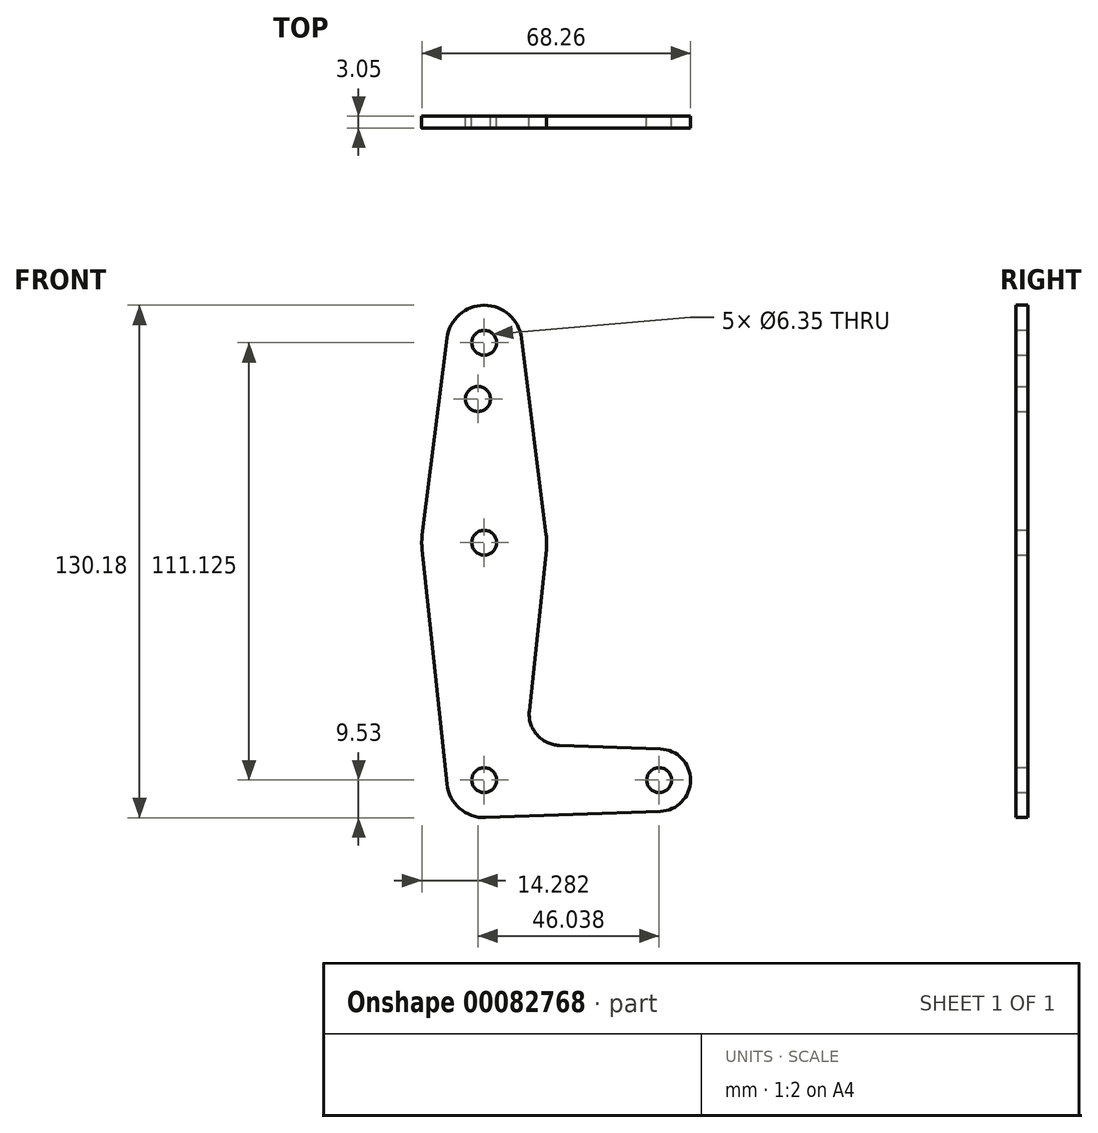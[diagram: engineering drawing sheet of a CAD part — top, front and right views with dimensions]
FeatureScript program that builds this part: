
annotation { "Feature Type Name" : "Feature", "Feature Type Description" : "" }
export const myFeature = defineFeature(function(context is Context, id is Id, definition is map)
    precondition{}
    {
        {
            var Q0;
            Q0=qCreatedBy(makeId("Front.planeOp"),FACE);
            var sketch = newSketch(context, id + "F0", { "sketchPlane" : qUnion([Q0])});
            skCircle(sketch, "E0", {"center": v(0, 111.13) * mm, "radius": 9.52 * mm});
            skCircle(sketch, "E1", {"center": v(0, 60.33) * mm, "radius": 15.88 * mm});
            skCircle(sketch, "E2", {"center": v(0, 0) * mm, "radius": 9.53 * mm});
            skCircle(sketch, "E3", {"center": v(44.45, 0) * mm, "radius": 7.94 * mm});
            skLineSegment(sketch, "E4", {"start": v(0, 111.13) * mm, "end": v(0, -3.17) * mm, "construction": true});
            skLineSegment(sketch, "E5", {"start": v(0, 60.33) * mm, "end": v(0, -3.18) * mm, "construction": true});
            skLineSegment(sketch, "E6", {"start": v(0, 0) * mm, "end": v(44.45, 0) * mm, "construction": true});
            skLineSegment(sketch, "E7", {"start": v(-15.79, 58.65) * mm, "end": v(-9.47, -1) * mm});
            skLineSegment(sketch, "E8", {"start": v(-9.47, -1) * mm, "end": v(-12.4, 26.68) * mm});
            skLineSegment(sketch, "E9", {"start": v(9.45, 112.32) * mm, "end": v(15.75, 62.3) * mm});
            skLineSegment(sketch, "E10", {"start": v(15.79, 58.65) * mm, "end": v(11.44, 17.63) * mm});
            skLineSegment(sketch, "E11", {"start": v(19.07, 8.85) * mm, "end": v(44.73, 7.93) * mm});
            skLineSegment(sketch, "E12", {"start": v(0.34, -9.52) * mm, "end": v(44.73, -7.93) * mm});
            skCircle(sketch, "E13", {"center": v(0, 60.33) * mm, "radius": 0.51 * mm});
            skCircle(sketch, "E14", {"center": v(0, 0) * mm, "radius": 0.51 * mm});
            skCircle(sketch, "E15", {"center": v(44.45, 0) * mm, "radius": 0.51 * mm});
            skCircle(sketch, "E16", {"center": v(0, 111.13) * mm, "radius": 0.51 * mm});
            skLineSegment(sketch, "E17", {"start": v(-9.45, 112.32) * mm, "end": v(-15.75, 62.3) * mm});
            skCircle(sketch, "E18", {"center": v(-1.59, 96.85) * mm, "radius": 3.18 * mm});
            skArc(sketch, "E19.filletArc", {"start": v(11.44, 17.63) * mm, "mid": v(13.35, 11.58) * mm, "end": v(19.07, 8.85) * mm});
            skCircle(sketch, "E20", {"center": v(0, 60.33) * mm, "radius": 3.18 * mm});
            skCircle(sketch, "E21", {"center": v(0, 111.13) * mm, "radius": 3.18 * mm});
            skCircle(sketch, "E22", {"center": v(0, 0) * mm, "radius": 3.18 * mm});
            skCircle(sketch, "E23", {"center": v(44.45, 0) * mm, "radius": 3.18 * mm});
            skSolve(sketch);
        }
        {
            var Q0;
            Q0 = qSketchRegion(id + "F0", true);
            extrude(context, id + "F1", {"entities" : qUnion([Q0]), "depth" : 3.05 * mm});
        }
    });
